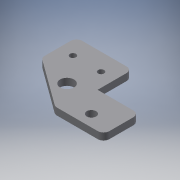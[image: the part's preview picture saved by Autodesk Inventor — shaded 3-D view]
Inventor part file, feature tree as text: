
AUTODESK INVENTOR PART (.ipt)
format: ipt  version: 2017 (Build 210142000, 142)  size: 239,616 bytes
history: native  units: mm
features: sketch x2, extrude x1, hole x1, projected_geometry x1
ambient origin geometry x8: Origin, YZ Plane, XZ Plane, XY Plane, X Axis, Y Axis, Z Axis, Center Point
bodies: Solid1 (feature_tree)
feature tree (5):
  extrude  "Extrusion1"  [1 undecoded]
  hole  "Hole1"  [1 undecoded]
  sketch  "Sketch1"  dims[d0=6.0mm d1=0.0mm]
  sketch  "Sketch2"  dims[d2=5.2mm d3=6.0mm d4=4.0mm d5=2.0mm d6=90.0deg d7=8.0mm d8=20.594885mm]
  projected_geometry  "Projected Loop1"
note: 2 required parameter values undecoded (feature->parameter linkage not recoverable at this tier; creation-order binding heuristic only, values carry confidence <= 0.55)
